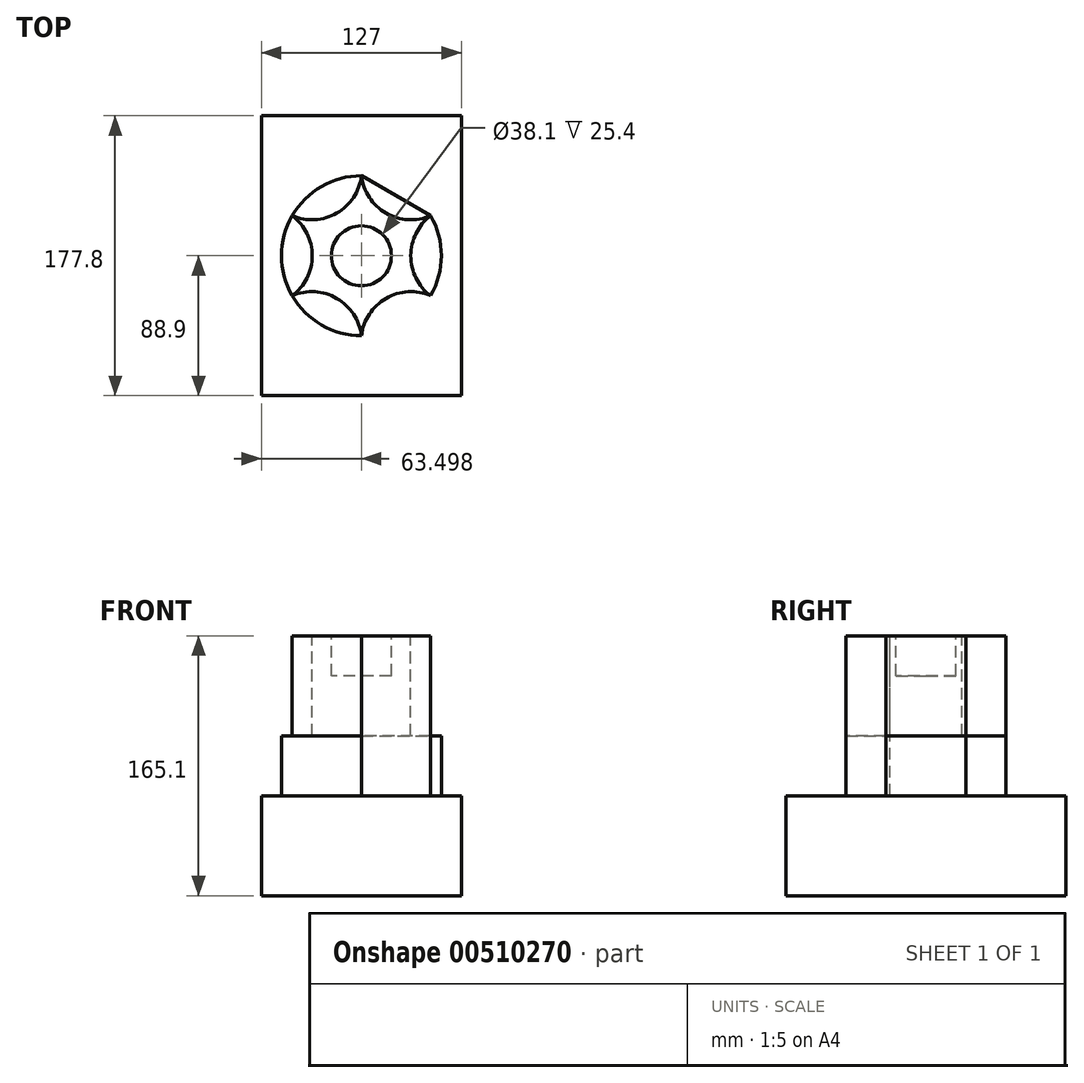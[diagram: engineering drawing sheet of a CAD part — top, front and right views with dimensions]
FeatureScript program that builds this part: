
annotation { "Feature Type Name" : "Feature", "Feature Type Description" : "" }
export const myFeature = defineFeature(function(context is Context, id is Id, definition is map)
    precondition{}
    {
        {
            var Q0;
            Q0=qCreatedBy(makeId("Front.planeOp"),FACE);
            var sketch = newSketch(context, id + "F0", { "sketchPlane" : qUnion([Q0])});
            skLineSegment(sketch, "E0.bottom", {"start": v(-68.45, 17.39) * mm, "end": v(58.55, 17.39) * mm});
            skLineSegment(sketch, "E0.top", {"start": v(-68.45, -46.11) * mm, "end": v(58.55, -46.11) * mm});
            skLineSegment(sketch, "E0.left", {"start": v(-68.45, 17.39) * mm, "end": v(-68.45, -46.11) * mm});
            skLineSegment(sketch, "E0.right", {"start": v(58.55, 17.39) * mm, "end": v(58.55, -46.11) * mm});
            skSolve(sketch);
        }
        {
            var Q0;
            Q0 = qSketchRegion(id + "F0", true);
            var Q1;
            Q1=makeQuery(id+"F0.imprint","IMPRINT",FACE,{"disambiguationData":[TD([[makeQuery(id+"F0.imprint","IMPRINT",EDGE,{"derivedFrom":sQuery(id+"F0.wireOp",EDGE,"E0.bottom")}),-1.0]])]});
            extrude(context, id + "F1", {"entities" : qUnion([Q0, Q1]), "depth" : 177.8 * mm});
        }
        {
            var Q0;
            Q0=makeQuery(id+"F1.opExtrude","SWEPT_FACE",FACE,{"disambiguationData":[OSD([sQuery(id+"F0.wireOp",EDGE,"E0.bottom")])]});
            var sketch = newSketch(context, id + "F2", { "sketchPlane" : qUnion([Q0])});
            skCircle(sketch, "E1", {"center": v(-4.95, -88.9) * mm, "radius": 50.8 * mm});
            skPoint(sketch, "E1.centerSnap0", {"position": v(-68.45, -88.9) * mm});
            skPoint(sketch, "E1.centerSnap1", {"position": v(-4.95, 0) * mm});
            skSolve(sketch);
        }
        {
            var Q0;
            Q0=makeQuery(id+"F2.imprint","IMPRINT",FACE,{"disambiguationData":[TD([[makeQuery(id+"F2.imprint","IMPRINT",EDGE,{"derivedFrom":sQuery(id+"F2.wireOp",EDGE,"E1")}),1.0]])]});
            extrude(context, id + "F3", {"entities" : qUnion([Q0]), "operationType" : NewBodyOperationType.ADD, "depth" : 101.6 * mm});
        }
        {
            var Q0;
            Q0=makeQuery(id+"F3.opExtrude","CAP_FACE",FACE,{"disambiguationData":[OSD([sQuery(id+"F2.wireOp",EDGE,"E1")])],"isStart":false});
            var sketch = newSketch(context, id + "F4", { "sketchPlane" : qUnion([Q0])});
            skPoint(sketch, "E2", {"position": v(-4.95, -38.1) * mm});
            skPoint(sketch, "E3", {"position": v(-4.95, -88.9) * mm});
            skPoint(sketch, "E4.1.0", {"position": v(-48.95, -63.5) * mm});
            skPoint(sketch, "E4.2.0", {"position": v(-48.95, -114.3) * mm});
            skPoint(sketch, "E4.3.0", {"position": v(-4.95, -139.7) * mm});
            skPoint(sketch, "E4.4.0", {"position": v(39.04, -114.3) * mm});
            skPoint(sketch, "E4.5.0", {"position": v(39.04, -63.5) * mm});
            skArc(sketch, "E5", {"start": v(-48.95, -63.5) * mm, "mid": v(-20.6, -61.8) * mm, "end": v(-4.95, -38.1) * mm});
            skArc(sketch, "E6", {"start": v(-4.95, -38.1) * mm, "mid": v(10.7, -61.8) * mm, "end": v(39.04, -63.5) * mm});
            skArc(sketch, "E7", {"start": v(39.04, -63.5) * mm, "mid": v(26.34, -88.9) * mm, "end": v(39.04, -114.3) * mm});
            skArc(sketch, "E8", {"start": v(39.04, -114.3) * mm, "mid": v(10.7, -116) * mm, "end": v(-4.95, -139.7) * mm});
            skArc(sketch, "E9", {"start": v(-4.95, -139.7) * mm, "mid": v(-20.6, -116) * mm, "end": v(-48.95, -114.3) * mm});
            skArc(sketch, "E10", {"start": v(-48.95, -114.3) * mm, "mid": v(-36.25, -88.9) * mm, "end": v(-48.95, -63.5) * mm});
            skCircle(sketch, "E11", {"center": v(-4.95, -88.9) * mm, "radius": 50.8 * mm});
            skSolve(sketch);
        }
        {
            var Q0;
            {var subQ0=sQuery(id+"F4.wireOp",EDGE,"E5");Q0=makeQuery(id+"F4.imprint","IMPRINT",FACE,{"disambiguationData":[TD([[makeQuery(id+"F4.imprint","IMPRINT",EDGE,{"derivedFrom":subQ0}),1.0]])]});}
            var Q1;
            {var subQ0=sQuery(id+"F4.wireOp",EDGE,"E6");Q1=makeQuery(id+"F4.imprint","IMPRINT",FACE,{"disambiguationData":[TD([[makeQuery(id+"F4.imprint","IMPRINT",EDGE,{"derivedFrom":subQ0}),1.0]])]});}
            var Q2;
            {var subQ0=sQuery(id+"F4.wireOp",EDGE,"E7");Q2=makeQuery(id+"F4.imprint","IMPRINT",FACE,{"disambiguationData":[TD([[makeQuery(id+"F4.imprint","IMPRINT",EDGE,{"derivedFrom":subQ0}),1.0]])]});}
            var Q3;
            {var subQ0=sQuery(id+"F4.wireOp",EDGE,"E8");Q3=makeQuery(id+"F4.imprint","IMPRINT",FACE,{"disambiguationData":[TD([[makeQuery(id+"F4.imprint","IMPRINT",EDGE,{"derivedFrom":subQ0}),1.0]])]});}
            var Q4;
            {var subQ0=sQuery(id+"F4.wireOp",EDGE,"E9");Q4=makeQuery(id+"F4.imprint","IMPRINT",FACE,{"disambiguationData":[TD([[makeQuery(id+"F4.imprint","IMPRINT",EDGE,{"derivedFrom":subQ0}),1.0]])]});}
            var Q5;
            {var subQ0=sQuery(id+"F4.wireOp",EDGE,"E10");Q5=makeQuery(id+"F4.imprint","IMPRINT",FACE,{"disambiguationData":[TD([[makeQuery(id+"F4.imprint","IMPRINT",EDGE,{"derivedFrom":subQ0}),1.0]])]});}
            extrude(context, id + "F5", {"entities" : qUnion([Q0, Q1, Q2, Q3, Q4, Q5]), "operationType" : NewBodyOperationType.REMOVE, "oppositeDirection" : true, "depth" : 63.5 * mm});
        }
        {
            var Q0;
            Q0=makeQuery(id+"F3.opExtrude","CAP_FACE",FACE,{"disambiguationData":[OSD([sQuery(id+"F2.wireOp",EDGE,"E1")])],"isStart":false});
            var sketch = newSketch(context, id + "F6", { "sketchPlane" : qUnion([Q0])});
            skCircle(sketch, "E12", {"center": v(-4.95, -88.9) * mm, "radius": 19.05 * mm});
            skSolve(sketch);
        }
        {
            var Q0;
            Q0=makeQuery(id+"F6.imprint","IMPRINT",FACE,{"disambiguationData":[TD([[makeQuery(id+"F6.imprint","IMPRINT",EDGE,{"derivedFrom":sQuery(id+"F6.wireOp",EDGE,"E12")}),1.0]])]});
            extrude(context, id + "F7", {"entities" : qUnion([Q0]), "operationType" : NewBodyOperationType.REMOVE, "oppositeDirection" : true, "depth" : 25.4 * mm});
        }
        {
            var Q0;
            Q0=makeQuery(id+"F5.boolean.opBoolean","COPY",FACE,{"derivedFrom":makeQuery(id+"F5.opExtrude","CAP_FACE",FACE,{"disambiguationData":[OSD([sQuery(id+"F4.wireOp",EDGE,"E8"),sQuery(id+"F4.wireOp",EDGE,"E11")])],"isStart":false})});
            var sketch = newSketch(context, id + "F8", { "sketchPlane" : qUnion([Q0])});
            skArc(sketch, "E13", {"start": v(39.04, -114.3) * mm, "mid": v(10.7, -116) * mm, "end": v(-4.95, -139.7) * mm});
            skArc(sketch, "E14", {"start": v(-4.95, -139.7) * mm, "mid": v(20.45, -132.9) * mm, "end": v(39.04, -114.3) * mm});
            skSolve(sketch);
        }
        {
            var Q0;
            Q0=makeQuery(id+"F8.imprint","IMPRINT",FACE,{"disambiguationData":[TD([[makeQuery(id+"F8.imprint","IMPRINT",EDGE,{"derivedFrom":sQuery(id+"F8.wireOp",EDGE,"E13")}),1.0]])]});
            extrude(context, id + "F9", {"entities" : qUnion([Q0]), "operationType" : NewBodyOperationType.REMOVE, "oppositeDirection" : true, "depth" : 38.1 * mm});
        }
        {
            var Q0;
            Q0=makeQuery(id+"F5.boolean.opBoolean","COPY",FACE,{"derivedFrom":makeQuery(id+"F5.opExtrude","CAP_FACE",FACE,{"disambiguationData":[OSD([sQuery(id+"F4.wireOp",EDGE,"E6"),sQuery(id+"F4.wireOp",EDGE,"E11")])],"isStart":false})});
            var sketch = newSketch(context, id + "F10", { "sketchPlane" : qUnion([Q0])});
            skLineSegment(sketch, "E15", {"start": v(39.04, -63.5) * mm, "end": v(-4.95, -38.1) * mm});
            skArc(sketch, "E16", {"start": v(39.04, -63.5) * mm, "mid": v(20.45, -44.9) * mm, "end": v(-4.95, -38.1) * mm});
            skSolve(sketch);
        }
        {
            var Q0;
            Q0=makeQuery(id+"F10.imprint","IMPRINT",FACE,{"disambiguationData":[TD([[makeQuery(id+"F10.imprint","IMPRINT",EDGE,{"derivedFrom":sQuery(id+"F10.wireOp",EDGE,"E15")}),-1.0]])]});
            extrude(context, id + "F11", {"entities" : qUnion([Q0]), "operationType" : NewBodyOperationType.REMOVE, "oppositeDirection" : true, "depth" : 38.1 * mm, "offsetDistance" : 25.4 * mm});
        }
    });
